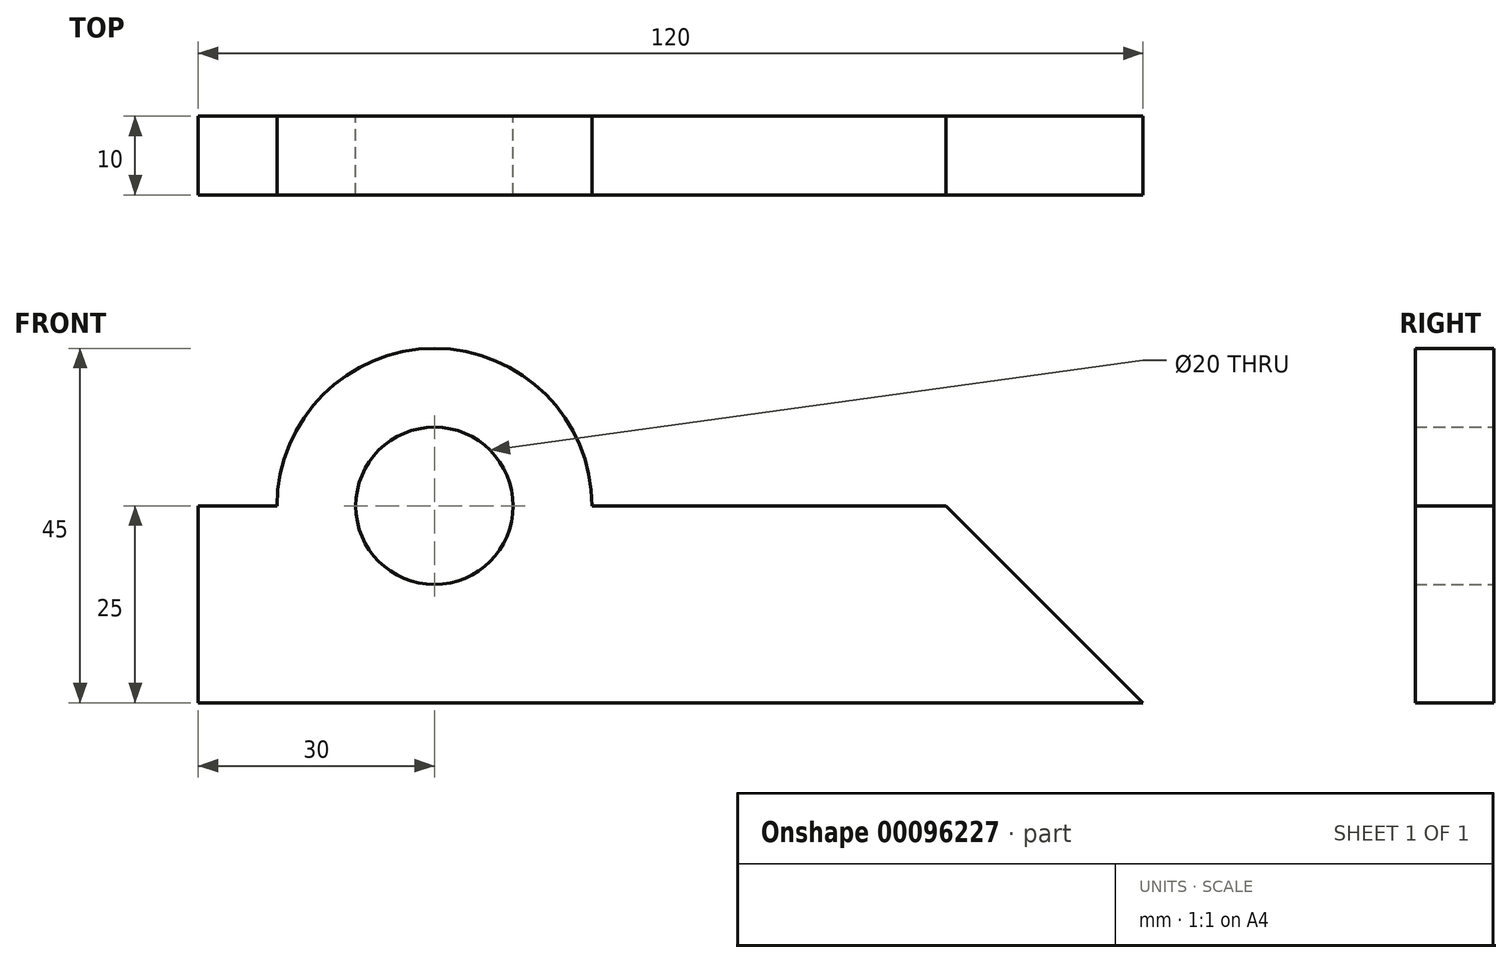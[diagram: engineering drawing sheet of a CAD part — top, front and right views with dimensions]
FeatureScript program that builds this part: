
annotation { "Feature Type Name" : "Feature", "Feature Type Description" : "" }
export const myFeature = defineFeature(function(context is Context, id is Id, definition is map)
    precondition{}
    {
        {
            var Q0;
            Q0=qCreatedBy(makeId("Front.planeOp"),FACE);
            var sketch = newSketch(context, id + "F0", { "sketchPlane" : qUnion([Q0])});
            skLineSegment(sketch, "E0", {"start": v(0, 0) * mm, "end": v(120, 0) * mm});
            skLineSegment(sketch, "E1", {"start": v(120, 0) * mm, "end": v(95, 25) * mm});
            skLineSegment(sketch, "E2", {"start": v(0, 25) * mm, "end": v(0, 0) * mm});
            skLineSegment(sketch, "E3", {"start": v(0, 25) * mm, "end": v(30, 25) * mm, "construction": true});
            skCircle(sketch, "E4", {"center": v(30, 25) * mm, "radius": 10 * mm});
            skLineSegment(sketch, "E5", {"start": v(0, 25) * mm, "end": v(10, 25) * mm});
            skArc(sketch, "E6", {"start": v(10, 25) * mm, "mid": v(30, 45) * mm, "end": v(50, 25) * mm});
            skLineSegment(sketch, "E7", {"start": v(95, 25) * mm, "end": v(50, 25) * mm});
            skSolve(sketch);
        }
        {
            var Q0;
            Q0=makeQuery(id+"F0.imprint","IMPRINT",FACE,{"disambiguationData":[TD([[makeQuery(id+"F0.imprint","IMPRINT",EDGE,{"derivedFrom":sQuery(id+"F0.wireOp",EDGE,"E0")}),1.0]])]});
            extrude(context, id + "F1", {"entities" : qUnion([Q0]), "depth" : 10 * mm});
        }
    });
